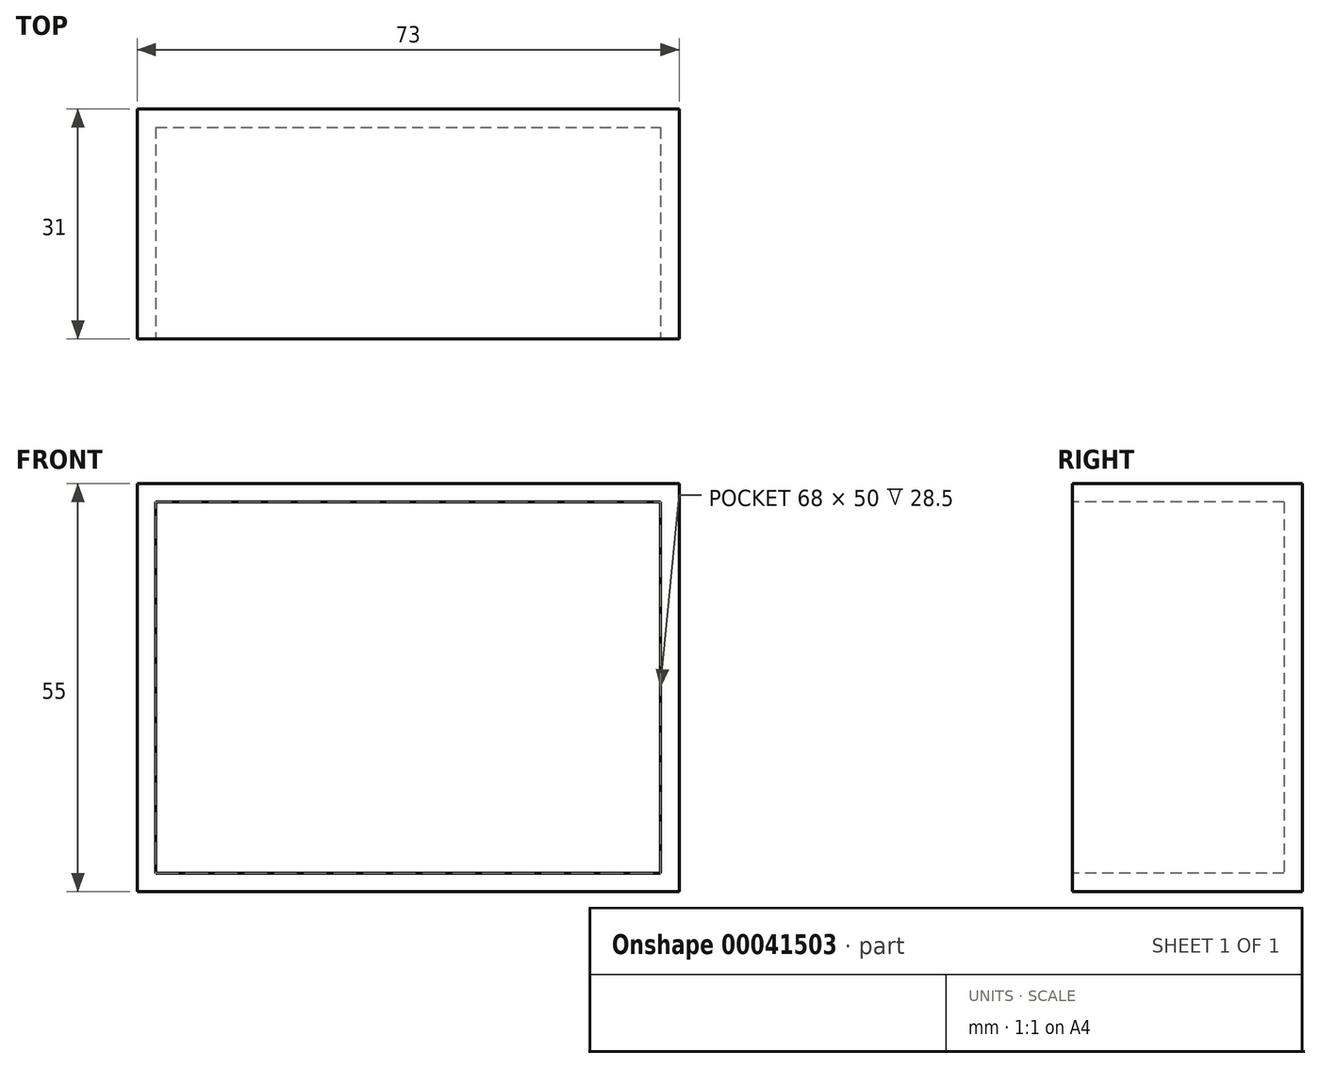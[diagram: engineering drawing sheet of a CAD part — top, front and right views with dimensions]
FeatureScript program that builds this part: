
annotation { "Feature Type Name" : "Feature", "Feature Type Description" : "" }
export const myFeature = defineFeature(function(context is Context, id is Id, definition is map)
    precondition{}
    {
        {
            assignVariable(context, id + "F0", {"name" : "ShellWidth", "anyValue" : 2.5});
        }
        {
            assignVariable(context, id + "F1", {"name" : "Heigth", "anyValue" : 50 + (getVariable(context, 'ShellWidth') * 2)});
        }
        {
            var Q0;
            Q0=qCreatedBy(makeId("Top.planeOp"),FACE);
            var sketch = newSketch(context, id + "F2", { "sketchPlane" : qUnion([Q0])});
            skLineSegment(sketch, "E0.bottom", {"start": v(-24.49, 12.79) * mm, "end": v(48.51, 12.79) * mm});
            skLineSegment(sketch, "E0.top", {"start": v(-24.49, -18.21) * mm, "end": v(48.51, -18.21) * mm});
            skLineSegment(sketch, "E0.left", {"start": v(-24.49, 12.79) * mm, "end": v(-24.49, -18.21) * mm});
            skLineSegment(sketch, "E0.right", {"start": v(48.51, 12.79) * mm, "end": v(48.51, -18.21) * mm});
            skSolve(sketch);
        }
        {
            var Q0;
            Q0=makeQuery(id+"F2.imprint","IMPRINT",FACE,{"disambiguationData":[TD([[makeQuery(id+"F2.imprint","IMPRINT",EDGE,{"derivedFrom":sQuery(id+"F2.wireOp",EDGE,"E0.bottom")}),-1.0]])]});
            extrude(context, id + "F3", {"entities" : qUnion([Q0]), "depth" : (getVariable(context, 'Heigth')) * mm});
        }
        {
            var Q0;
            Q0=makeQuery(id+"F3.opExtrude","SWEPT_FACE",FACE,{"disambiguationData":[OSD([sQuery(id+"F2.wireOp",EDGE,"E0.top")])]});
            shell(context, id + "F4", {"entities" : qUnion([Q0]), "thickness" : (getVariable(context, 'ShellWidth')) * mm});
        }
    });
